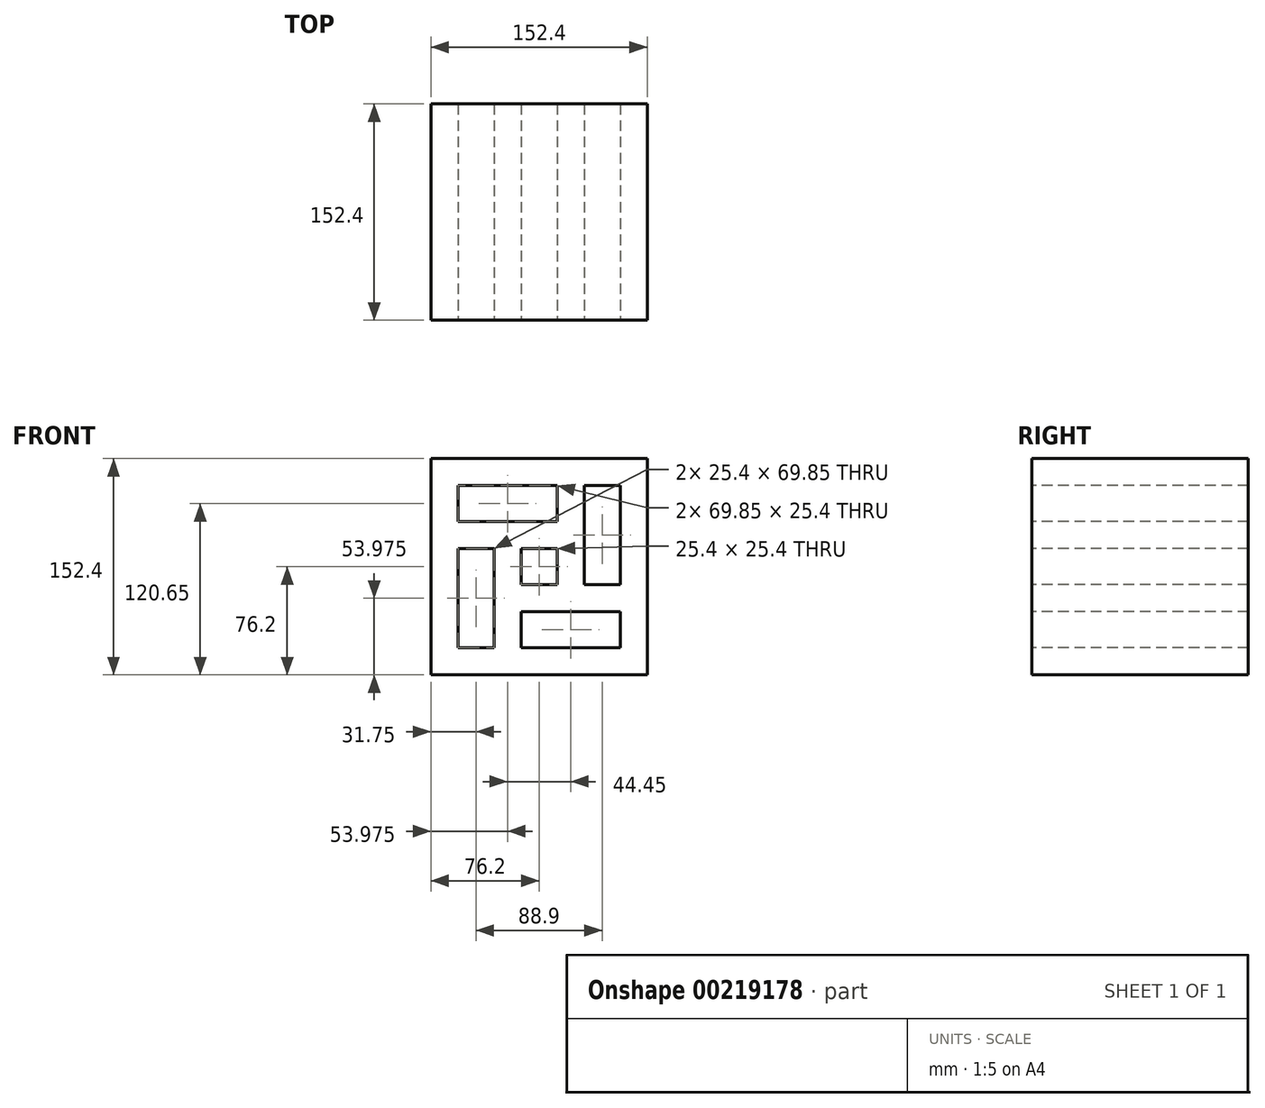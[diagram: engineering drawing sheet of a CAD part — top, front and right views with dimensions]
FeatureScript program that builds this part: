
annotation { "Feature Type Name" : "Feature", "Feature Type Description" : "" }
export const myFeature = defineFeature(function(context is Context, id is Id, definition is map)
    precondition{}
    {
        {
            var Q0;
            Q0=qCreatedBy(makeId("Top.planeOp"),FACE);
            var sketch = newSketch(context, id + "F2", { "sketchPlane" : qUnion([Q0])});
            skLineSegment(sketch, "E0.bottom", {"start": v(76.2, 76.2) * mm, "end": v(-76.2, 76.2) * mm});
            skLineSegment(sketch, "E0.top", {"start": v(76.2, -76.2) * mm, "end": v(-76.2, -76.2) * mm});
            skLineSegment(sketch, "E0.left", {"start": v(76.2, 76.2) * mm, "end": v(76.2, -76.2) * mm});
            skLineSegment(sketch, "E0.right", {"start": v(-76.2, 76.2) * mm, "end": v(-76.2, -76.2) * mm});
            skPoint(sketch, "E0.middle", {"position": v(0, 0) * mm});
            skSolve(sketch);
        }
        {
            var Q0;
            Q0=makeQuery(id+"F2.imprint","IMPRINT",FACE,{"disambiguationData":[TD([[makeQuery(id+"F2.imprint","IMPRINT",EDGE,{"derivedFrom":sQuery(id+"F2.wireOp",EDGE,"E0.bottom")}),1.0]])]});
            extrude(context, id + "F0", {"entities" : qUnion([Q0]), "endBound" : BoundingType.SYMMETRIC, "depth" : 152.4 * mm});
        }
        {
            var Q0;
            Q0=makeQuery(id+"F0.opExtrude","SWEPT_FACE",FACE,{"disambiguationData":[OSD([sQuery(id+"F2.wireOp",EDGE,"E0.top")])]});
            var sketch = newSketch(context, id + "F3", { "sketchPlane" : qUnion([Q0])});
            skLineSegment(sketch, "E1.bottom", {"start": v(12.7, -12.7) * mm, "end": v(-12.7, -12.7) * mm});
            skLineSegment(sketch, "E1.top", {"start": v(12.7, 12.7) * mm, "end": v(-12.7, 12.7) * mm});
            skLineSegment(sketch, "E1.left", {"start": v(12.7, -12.7) * mm, "end": v(12.7, 12.7) * mm});
            skLineSegment(sketch, "E1.right", {"start": v(-12.7, -12.7) * mm, "end": v(-12.7, 12.7) * mm});
            skPoint(sketch, "E1.middle", {"position": v(0, 0) * mm});
            skLineSegment(sketch, "E2.bottom", {"start": v(31.75, 57.15) * mm, "end": v(57.15, 57.15) * mm});
            skLineSegment(sketch, "E2.top", {"start": v(31.75, -12.7) * mm, "end": v(57.15, -12.7) * mm});
            skLineSegment(sketch, "E2.left", {"start": v(31.75, 57.15) * mm, "end": v(31.75, -12.7) * mm});
            skLineSegment(sketch, "E2.right", {"start": v(57.15, 57.15) * mm, "end": v(57.15, -12.7) * mm});
            skLineSegment(sketch, "E3.bottom", {"start": v(57.15, -57.15) * mm, "end": v(-12.7, -57.15) * mm});
            skLineSegment(sketch, "E3.top", {"start": v(57.15, -31.75) * mm, "end": v(-12.7, -31.75) * mm});
            skLineSegment(sketch, "E3.left", {"start": v(57.15, -57.15) * mm, "end": v(57.15, -31.75) * mm});
            skLineSegment(sketch, "E3.right", {"start": v(-12.7, -57.15) * mm, "end": v(-12.7, -31.75) * mm});
            skLineSegment(sketch, "E4.bottom", {"start": v(-31.75, -57.15) * mm, "end": v(-57.15, -57.15) * mm});
            skLineSegment(sketch, "E4.top", {"start": v(-31.75, 12.7) * mm, "end": v(-57.15, 12.7) * mm});
            skLineSegment(sketch, "E4.left", {"start": v(-31.75, -57.15) * mm, "end": v(-31.75, 12.7) * mm});
            skLineSegment(sketch, "E4.right", {"start": v(-57.15, -57.15) * mm, "end": v(-57.15, 12.7) * mm});
            skLineSegment(sketch, "E5.bottom", {"start": v(-57.15, 57.15) * mm, "end": v(12.7, 57.15) * mm});
            skLineSegment(sketch, "E5.top", {"start": v(-57.15, 31.75) * mm, "end": v(12.7, 31.75) * mm});
            skLineSegment(sketch, "E5.left", {"start": v(-57.15, 31.75) * mm, "end": v(-57.15, 57.15) * mm});
            skLineSegment(sketch, "E5.right", {"start": v(12.7, 31.75) * mm, "end": v(12.7, 57.15) * mm});
            skSolve(sketch);
        }
        {
            var Q0;
            Q0=makeQuery(id+"F3.imprint","IMPRINT",FACE,{"disambiguationData":[TD([[makeQuery(id+"F3.imprint","IMPRINT",EDGE,{"derivedFrom":sQuery(id+"F3.wireOp",EDGE,"E5.bottom")}),-1.0]])]});
            var Q1;
            Q1=makeQuery(id+"F3.imprint","IMPRINT",FACE,{"disambiguationData":[TD([[makeQuery(id+"F3.imprint","IMPRINT",EDGE,{"derivedFrom":sQuery(id+"F3.wireOp",EDGE,"E2.bottom")}),-1.0]])]});
            var Q2;
            Q2=makeQuery(id+"F3.imprint","IMPRINT",FACE,{"disambiguationData":[TD([[makeQuery(id+"F3.imprint","IMPRINT",EDGE,{"derivedFrom":sQuery(id+"F3.wireOp",EDGE,"E4.bottom")}),-1.0]])]});
            var Q3;
            Q3=makeQuery(id+"F3.imprint","IMPRINT",FACE,{"disambiguationData":[TD([[makeQuery(id+"F3.imprint","IMPRINT",EDGE,{"derivedFrom":sQuery(id+"F3.wireOp",EDGE,"E1.bottom")}),-1.0]])]});
            var Q4;
            Q4=makeQuery(id+"F3.imprint","IMPRINT",FACE,{"disambiguationData":[TD([[makeQuery(id+"F3.imprint","IMPRINT",EDGE,{"derivedFrom":sQuery(id+"F3.wireOp",EDGE,"E3.bottom")}),-1.0]])]});
            extrude(context, id + "F1", {"entities" : qUnion([Q0, Q1, Q2, Q3, Q4]), "operationType" : NewBodyOperationType.REMOVE, "endBound" : BoundingType.THROUGH_ALL, "oppositeDirection" : true, "depth" : 25.4 * mm});
        }
    });
